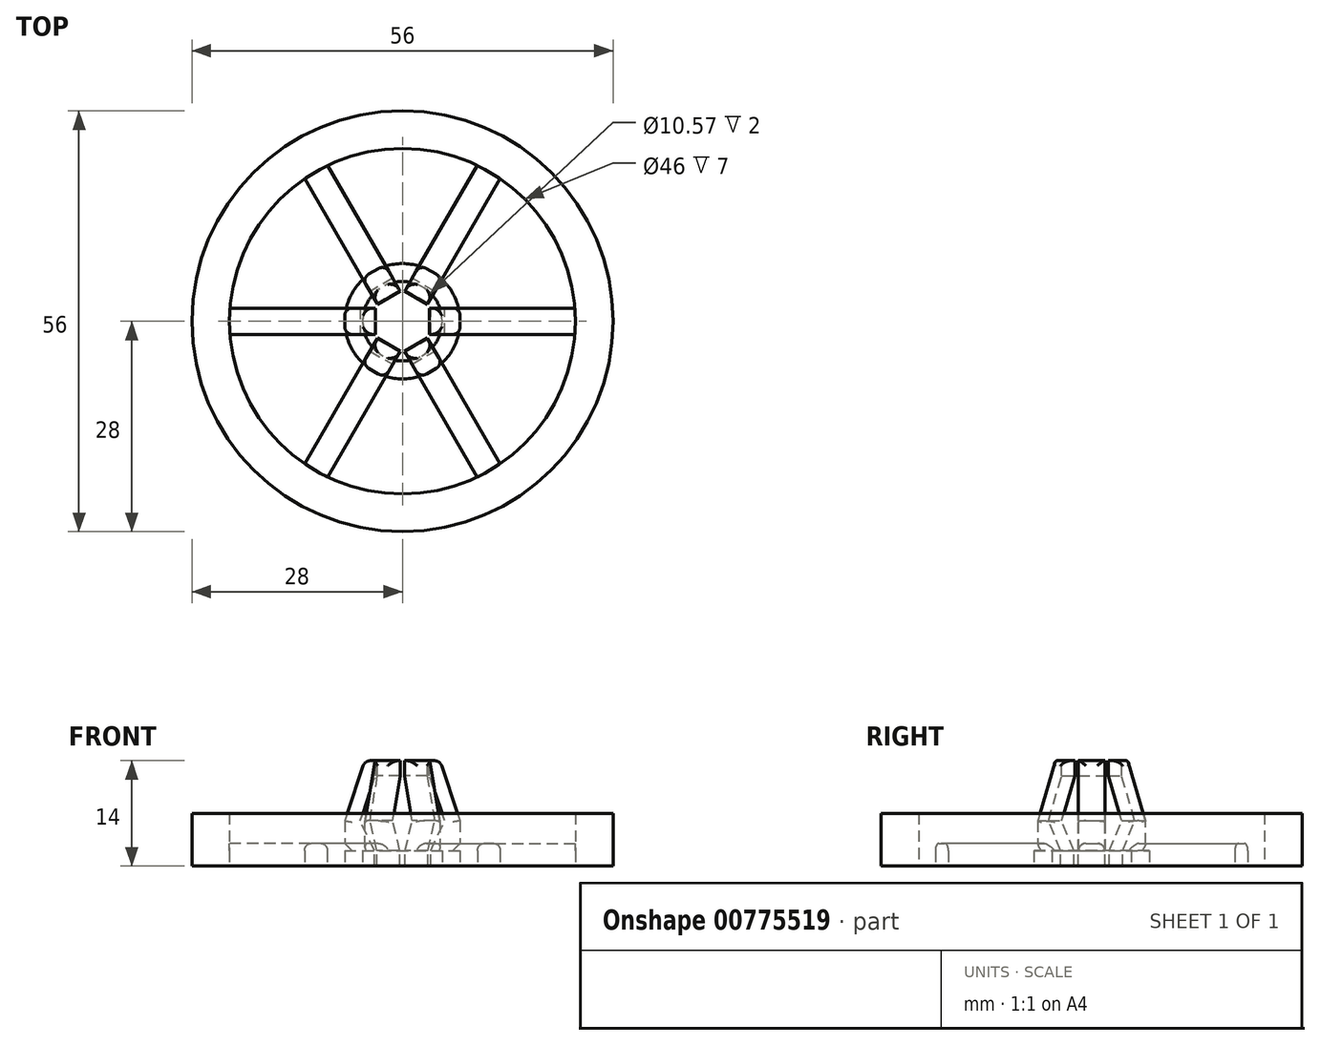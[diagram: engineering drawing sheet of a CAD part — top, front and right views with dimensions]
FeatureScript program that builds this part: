
annotation { "Feature Type Name" : "Feature", "Feature Type Description" : "" }
export const myFeature = defineFeature(function(context is Context, id is Id, definition is map)
    precondition{}
    {
        {
            var Q0;
            Q0=qCreatedBy(makeId("Front.planeOp"),FACE);
            var sketch = newSketch(context, id + "F0", { "sketchPlane" : qUnion([Q0])});
            skLineSegment(sketch, "E0", {"start": v(0, 0) * mm, "end": v(0, 15.23) * mm});
            skLineSegment(sketch, "E1", {"start": v(3.75, 0) * mm, "end": v(3.75, 2) * mm});
            skLineSegment(sketch, "E2", {"start": v(3.75, 2) * mm, "end": v(5.6, 6.02) * mm});
            skLineSegment(sketch, "E3", {"start": v(5.6, 6.02) * mm, "end": v(3.6, 12) * mm});
            skLineSegment(sketch, "E4", {"start": v(3.6, 12) * mm, "end": v(3.6, 14) * mm});
            skLineSegment(sketch, "E5", {"start": v(3.6, 14) * mm, "end": v(5, 14) * mm});
            skLineSegment(sketch, "E6", {"start": v(5, 14) * mm, "end": v(7.67, 6) * mm});
            skLineSegment(sketch, "E7", {"start": v(7.67, 6) * mm, "end": v(7.67, 0) * mm});
            skLineSegment(sketch, "E8", {"start": v(7.67, 0) * mm, "end": v(3.75, 0) * mm});
            skLineSegment(sketch, "E9", {"start": v(7.67, 0) * mm, "end": v(7.67, 3) * mm});
            skLineSegment(sketch, "E10", {"start": v(7.67, 3) * mm, "end": v(23, 3) * mm});
            skLineSegment(sketch, "E11", {"start": v(23, 3) * mm, "end": v(23, 0) * mm});
            skLineSegment(sketch, "E12", {"start": v(23, 0) * mm, "end": v(7.67, 0) * mm});
            skLineSegment(sketch, "E13", {"start": v(23, 0) * mm, "end": v(28, 0) * mm});
            skLineSegment(sketch, "E14", {"start": v(28, 0) * mm, "end": v(28, 7) * mm});
            skLineSegment(sketch, "E15", {"start": v(28, 7) * mm, "end": v(23, 7) * mm});
            skLineSegment(sketch, "E16", {"start": v(23, 7) * mm, "end": v(23, 3) * mm});
            skLineSegment(sketch, "E17", {"start": v(3.75, 2) * mm, "end": v(7.67, 2) * mm});
            skLineSegment(sketch, "E18", {"start": v(7.67, 2) * mm, "end": v(7.67, 0) * mm});
            skLineSegment(sketch, "E19", {"start": v(5.29, 2) * mm, "end": v(5.29, 0) * mm});
            skLineSegment(sketch, "E20", {"start": v(5.29, 0) * mm, "end": v(7.67, 0) * mm});
            skCircle(sketch, "E21", {"center": v(28, 0.88) * mm, "radius": 0.5 * mm});
            skSolve(sketch);
        }
        {
            var Q0;
            {var subQ0=sQuery(id+"F0.wireOp",EDGE,"E1");Q0=makeQuery(id+"F0.imprint","IMPRINT",FACE,{"disambiguationData":[TD([[makeQuery(id+"F0.imprint","IMPRINT",EDGE,{"derivedFrom":subQ0}),-1.0]])]});}
            var Q1;
            {var subQ0=sQuery(id+"F0.wireOp",EDGE,"E2");Q1=makeQuery(id+"F0.imprint","IMPRINT",FACE,{"disambiguationData":[TD([[makeQuery(id+"F0.imprint","IMPRINT",EDGE,{"derivedFrom":subQ0}),-1.0]])]});}
            var Q2;
            {var subQ5=sQuery(id+"F0.wireOp",EDGE,"E19");Q2=makeQuery(id+"F0.imprint","IMPRINT",FACE,{"disambiguationData":[TD([[makeQuery(id+"F0.imprint","IMPRINT",EDGE,{"derivedFrom":subQ5}),1.0]])]});}
            extrude(context, id + "F1", {"entities" : qUnion([Q0, Q1, Q2]), "endBound" : BoundingType.SYMMETRIC, "depth" : 3.5 * mm, "offsetDistance" : 25 * mm});
        }
        {
            var Q0;
            {var subQ0=sQuery(id+"F0.wireOp",EDGE,"E10");Q0=makeQuery(id+"F0.imprint","IMPRINT",FACE,{"disambiguationData":[TD([[makeQuery(id+"F0.imprint","IMPRINT",EDGE,{"derivedFrom":subQ0}),-1.0]])]});}
            extrude(context, id + "F2", {"entities" : qUnion([Q0]), "operationType" : NewBodyOperationType.ADD, "endBound" : BoundingType.SYMMETRIC, "depth" : 3.5 * mm, "offsetDistance" : 25 * mm});
        }
        {
            var Q0;
            Q0=makeQuery(id+"F0.imprint","IMPRINT",FACE,{"disambiguationData":[TD([[makeQuery(id+"F0.imprint","IMPRINT",EDGE,{"derivedFrom":sQuery(id+"F0.wireOp",EDGE,"E11")}),1.0]])]});
            var Q1;
            {var subQ0=sQuery(id+"F0.wireOp",EDGE,"E21");var subQ1=sQuery(id+"F0.wireOp",EDGE,"E14");var subQ2=makeQuery(id+"F0.imprint","INTERSECT",VERTEX,{"disambiguationData":[OD(0.0)],"derivedFrom":[subQ1,subQ0]});Q1=makeQuery(id+"F0.imprint","IMPRINT",FACE,{"disambiguationData":[TD([[makeQuery(id+"F0.imprint","IMPRINT",EDGE,{"disambiguationData":[TD([[subQ2,1.0]])],"derivedFrom":subQ1}),1.0]])]});}
            var Q2;
            Q2=sQuery(id+"F0.wireOp",EDGE,"E0");
            revolve(context, id + "F3", {"surfaceOperationType" : NewSurfaceOperationType.NEW, "entities" : qUnion([Q0, Q1]), "axis" : qUnion([Q2]), "revolveType" : RevolveType.FULL});
        }
        {
            var Q0;
            Q0=makeQuery(id+"F2.opExtrude","CAP_EDGE",EDGE,{"disambiguationData":[OSD([sQuery(id+"F0.wireOp",EDGE,"E10")])],"isStart":false});
            var Q1;
            Q1=makeQuery(id+"F2.opExtrude","CAP_EDGE",EDGE,{"disambiguationData":[OSD([sQuery(id+"F0.wireOp",EDGE,"E10")])],"isStart":true});
            var Q2;
            Q2=makeQuery(id+"F1.opExtrude","CAP_EDGE",EDGE,{"disambiguationData":[OSD([sQuery(id+"F0.wireOp",EDGE,"E7")])],"isStart":false});
            var Q3;
            Q3=makeQuery(id+"F1.opExtrude","CAP_EDGE",EDGE,{"disambiguationData":[OSD([sQuery(id+"F0.wireOp",EDGE,"E6")])],"isStart":false});
            var Q4;
            Q4=makeQuery(id+"F1.opExtrude","CAP_EDGE",EDGE,{"disambiguationData":[OSD([sQuery(id+"F0.wireOp",EDGE,"E6")])],"isStart":true});
            var Q5;
            Q5=makeQuery(id+"F1.opExtrude","CAP_EDGE",EDGE,{"disambiguationData":[OSD([sQuery(id+"F0.wireOp",EDGE,"E7")])],"isStart":true});
            var Q6;
            Q6=makeQuery(id+"F1.opExtrude","SWEPT_EDGE",EDGE,{"disambiguationData":[OSD([sQuery(id+"F0.wireOp",EDGE,"E5"),sQuery(id+"F0.wireOp",EDGE,"E6")])]});
            fillet(context, id + "F4", {"entities" : qUnion([Q0, Q1, Q2, Q3, Q4, Q5, Q6]), "radius" : 1 * mm, "tangentPropagation" : true, "allowEdgeOverflow" : false});
        }
        {
            var Q0;
            Q0=makeQuery(id+"F1.opExtrude","SWEPT_BODY",BODY,{"disambiguationData":[OSD([sQuery(id+"F0.wireOp",EDGE,"E1"),sQuery(id+"F0.wireOp",EDGE,"E2"),sQuery(id+"F0.wireOp",EDGE,"E3"),sQuery(id+"F0.wireOp",EDGE,"E4"),sQuery(id+"F0.wireOp",EDGE,"E5"),sQuery(id+"F0.wireOp",EDGE,"E6"),sQuery(id+"F0.wireOp",EDGE,"E7"),sQuery(id+"F0.wireOp",EDGE,"E8")])]});
            var Q1;
            Q1=sQuery(id+"F0.wireOp",EDGE,"E0");
            circularPattern(context, id + "F5", {"entities" : qUnion([Q0]), "axis" : qUnion([Q1]), "angle" : 360 * degree, "instanceCount" : 6, "equalSpace" : true});
        }
        {
            var Q0;
            {var subQ5=sQuery(id+"F0.wireOp",EDGE,"E19");Q0=makeQuery(id+"F0.imprint","IMPRINT",FACE,{"disambiguationData":[TD([[makeQuery(id+"F0.imprint","IMPRINT",EDGE,{"derivedFrom":subQ5}),1.0]])]});}
            var Q1;
            Q1=sQuery(id+"F0.wireOp",EDGE,"E0");
            revolve(context, id + "F6", {"surfaceOperationType" : NewSurfaceOperationType.NEW, "entities" : qUnion([Q0]), "axis" : qUnion([Q1]), "revolveType" : RevolveType.FULL});
        }
    });
